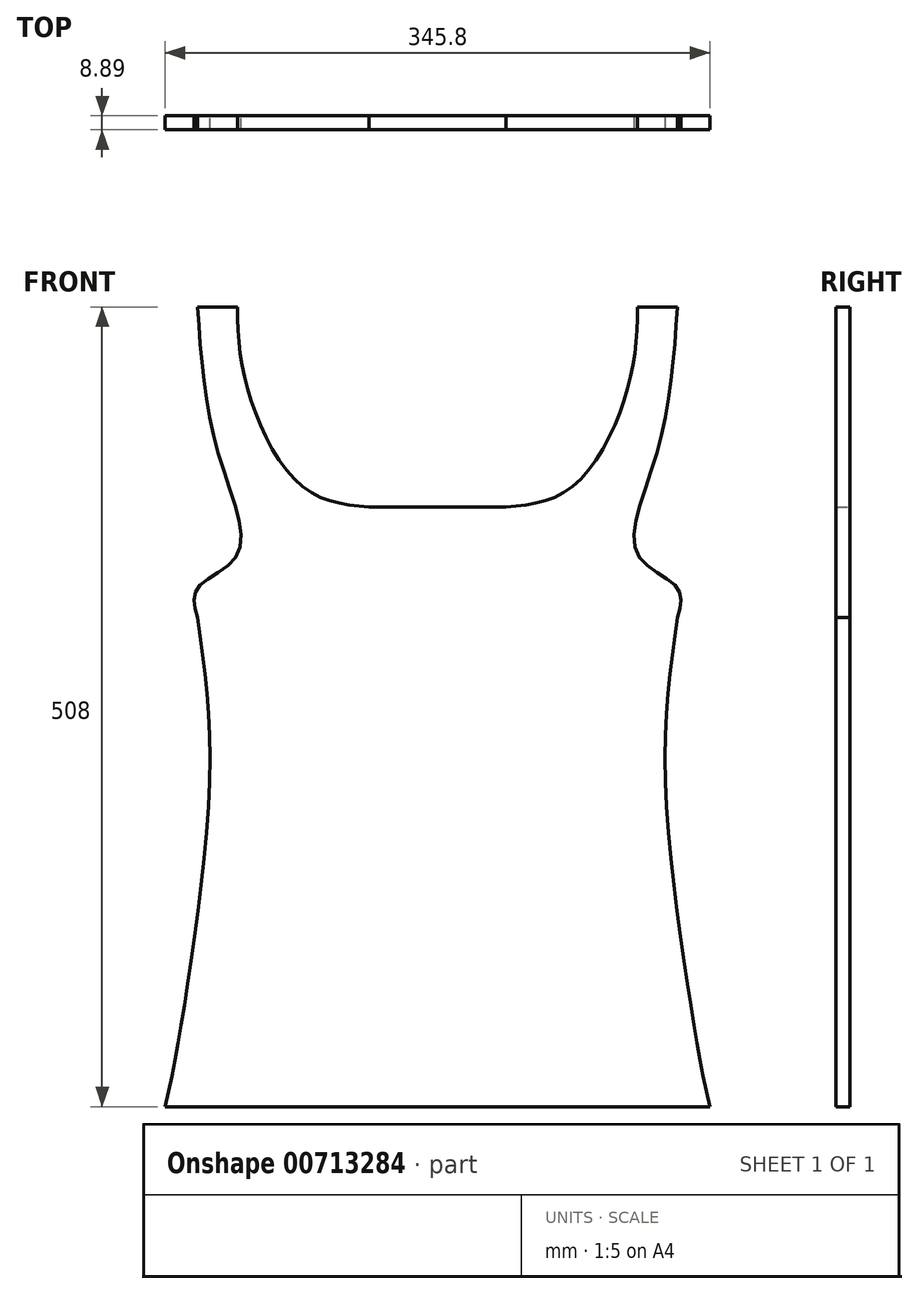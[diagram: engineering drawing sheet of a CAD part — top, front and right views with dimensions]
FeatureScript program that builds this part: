
annotation { "Feature Type Name" : "Feature", "Feature Type Description" : "" }
export const myFeature = defineFeature(function(context is Context, id is Id, definition is map)
    precondition{}
    {
        {
            var Q0;
            Q0=qCreatedBy(makeId("Front.planeOp"),FACE);
            var sketch = newSketch(context, id + "F0", { "sketchPlane" : qUnion([Q0])});
            skLineSegment(sketch, "E0.left", {"start": v(-228.6, 0) * mm, "end": v(-228.6, -508) * mm, "construction": true});
            skLineSegment(sketch, "E0.right", {"start": v(228.6, 0) * mm, "end": v(228.6, -508) * mm, "construction": true});
            skLineSegment(sketch, "E1", {"start": v(0, 249.25) * mm, "end": v(0, -566.39) * mm, "construction": true});
            skLineSegment(sketch, "E2", {"start": v(152.4, 0) * mm, "end": v(152.4, -508) * mm, "construction": true});
            skFitSpline(sketch, "E3", {"points": [v(127, 0) * mm, v(118.6, -59.09) * mm, v(83.81, -115.63) * mm, v(43.58, -127) * mm], "startDerivative": vector(0, -173.65) * mm, "endDerivative": vector(-145.04, -12.68) * mm});
            skFitSpline(sketch, "E4", {"points": [v(152.4, 0) * mm, v(139.27, -92.8) * mm, v(127, -157.2) * mm, v(152.4, -178.7) * mm, v(152.4, -197.18) * mm], "startDerivative": vector(-18.38, -270.65) * mm, "endDerivative": vector(-35.85, -127.26) * mm});
            skFitSpline(sketch, "E5", {"points": [v(152.4, -197.18) * mm, v(144.5, -293.22) * mm, v(160.04, -438.6) * mm, v(172.9, -508) * mm], "startDerivative": vector(-38.9, -271.92) * mm, "endDerivative": vector(51.84, -220.1) * mm});
            skLineSegment(sketch, "E6", {"start": v(172.9, -508) * mm, "end": v(0, -508) * mm});
            skLineSegment(sketch, "E7", {"start": v(43.58, -127) * mm, "end": v(0, -127) * mm});
            skFitSpline(sketch, "E8.MirrorCS", {"points": [v(-127, 0) * mm, v(-118.6, -59.09) * mm, v(-83.81, -115.63) * mm, v(-43.58, -127) * mm], "startDerivative": vector(0, -173.65) * mm, "endDerivative": vector(145.04, -12.68) * mm});
            skFitSpline(sketch, "E9.MirrorCS", {"points": [v(-152.4, 0) * mm, v(-139.27, -92.8) * mm, v(-127, -157.2) * mm, v(-152.4, -178.7) * mm, v(-152.4, -197.18) * mm], "startDerivative": vector(18.38, -270.65) * mm, "endDerivative": vector(35.85, -127.26) * mm});
            skFitSpline(sketch, "E10.MirrorCS", {"points": [v(-152.4, -197.18) * mm, v(-144.5, -293.22) * mm, v(-160.04, -438.6) * mm, v(-172.9, -508) * mm], "startDerivative": vector(38.9, -271.92) * mm, "endDerivative": vector(-51.84, -220.1) * mm});
            skLineSegment(sketch, "E11.MirrorCS", {"start": v(-43.58, -127) * mm, "end": v(0, -127) * mm});
            skLineSegment(sketch, "E12.MirrorCS", {"start": v(-172.9, -508) * mm, "end": v(0, -508) * mm});
            skLineSegment(sketch, "E13", {"start": v(152.4, 0) * mm, "end": v(127, 0) * mm});
            skLineSegment(sketch, "E14.MirrorCS", {"start": v(-152.4, 0) * mm, "end": v(-127, 0) * mm});
            skSolve(sketch);
        }
        {
            var Q0;
            Q0=qSketchRegion(id+"F0",true);
            extrude(context, id + "F1", {"entities" : qUnion([Q0]), "depth" : 8.9 * mm, "offsetDistance" : 25.4 * mm});
        }
    });
